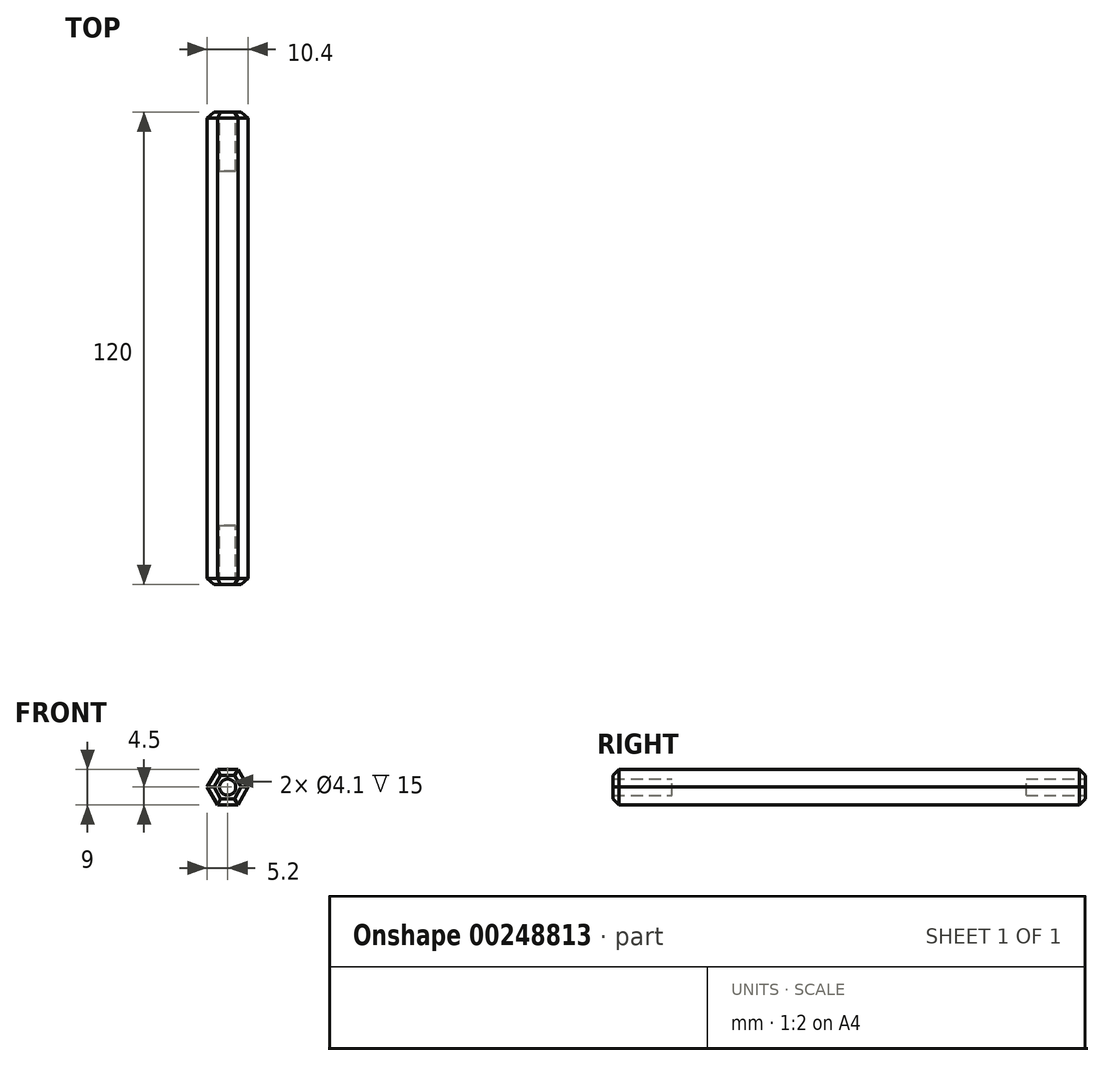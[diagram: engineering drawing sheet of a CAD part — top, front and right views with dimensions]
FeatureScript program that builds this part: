
annotation { "Feature Type Name" : "Feature", "Feature Type Description" : "" }
export const myFeature = defineFeature(function(context is Context, id is Id, definition is map)
    precondition{}
    {
        {
            assignVariable(context, id + "F0", {"name" : "length", "anyValue" : 120});
        }
        {
            var Q0;
            Q0=qCreatedBy(makeId("Front.planeOp"),FACE);
            var sketch = newSketch(context, id + "F1", { "sketchPlane" : qUnion([Q0])});
            skCircle(sketch, "E0.cCircle", {"center": v(0, 0) * mm, "radius": 4.5 * mm, "construction": true});
            skLineSegment(sketch, "E0.0", {"start": v(2.6, -4.5) * mm, "end": v(-2.6, -4.5) * mm});
            skLineSegment(sketch, "E0.1", {"start": v(-2.6, -4.5) * mm, "end": v(-5.2, 0) * mm});
            skLineSegment(sketch, "E0.2", {"start": v(-5.2, 0) * mm, "end": v(-2.6, 4.5) * mm});
            skLineSegment(sketch, "E0.3", {"start": v(-2.6, 4.5) * mm, "end": v(2.6, 4.5) * mm});
            skLineSegment(sketch, "E0.4", {"start": v(2.6, 4.5) * mm, "end": v(5.2, 0) * mm});
            skLineSegment(sketch, "E0.5", {"start": v(5.2, 0) * mm, "end": v(2.6, -4.5) * mm});
            skPoint(sketch, "E0.0.midPoint", {"position": v(0, -4.5) * mm});
            skCircle(sketch, "E1", {"center": v(0, 0) * mm, "radius": 2.05 * mm});
            skSolve(sketch);
        }
        {
            var Q0;
            Q0=makeQuery(id+"F1.imprint","IMPRINT",FACE,{"disambiguationData":[TD([[makeQuery(id+"F1.imprint","IMPRINT",EDGE,{"derivedFrom":sQuery(id+"F1.wireOp",EDGE,"E0.0")}),-1.0]])]});
            extrude(context, id + "F2", {"entities" : qUnion([Q0]), "depth" : (getVariable(context, 'length')) * mm, "symmetric" : true});
        }
        {
            var Q0;
            Q0=makeQuery(id+"F1.imprint","IMPRINT",FACE,{"disambiguationData":[TD([[makeQuery(id+"F1.imprint","IMPRINT",EDGE,{"derivedFrom":sQuery(id+"F1.wireOp",EDGE,"E1")}),1.0]])]});
            extrude(context, id + "F3", {"entities" : qUnion([Q0]), "operationType" : NewBodyOperationType.ADD, "depth" : (getVariable(context, 'length') - 30) * mm, "symmetric" : true});
        }
        {
            var Q0;
            Q0=makeQuery(id+"F2.opExtrude","CAP_EDGE",EDGE,{"disambiguationData":[OSD([sQuery(id+"F1.wireOp",EDGE,"E0.4")])],"isStart":false});
            var Q1;
            Q1=makeQuery(id+"F2.opExtrude","CAP_EDGE",EDGE,{"disambiguationData":[OSD([sQuery(id+"F1.wireOp",EDGE,"E0.3")])],"isStart":false});
            var Q2;
            Q2=makeQuery(id+"F2.opExtrude","CAP_EDGE",EDGE,{"disambiguationData":[OSD([sQuery(id+"F1.wireOp",EDGE,"E0.2")])],"isStart":false});
            var Q3;
            Q3=makeQuery(id+"F2.opExtrude","CAP_EDGE",EDGE,{"disambiguationData":[OSD([sQuery(id+"F1.wireOp",EDGE,"E0.1")])],"isStart":false});
            var Q4;
            Q4=makeQuery(id+"F2.opExtrude","CAP_EDGE",EDGE,{"disambiguationData":[OSD([sQuery(id+"F1.wireOp",EDGE,"E0.0")])],"isStart":false});
            var Q5;
            Q5=makeQuery(id+"F2.opExtrude","CAP_EDGE",EDGE,{"disambiguationData":[OSD([sQuery(id+"F1.wireOp",EDGE,"E0.5")])],"isStart":false});
            var Q6;
            Q6=makeQuery(id+"F2.opExtrude","CAP_EDGE",EDGE,{"disambiguationData":[OSD([sQuery(id+"F1.wireOp",EDGE,"E0.4")])],"isStart":true});
            var Q7;
            Q7=makeQuery(id+"F2.opExtrude","CAP_EDGE",EDGE,{"disambiguationData":[OSD([sQuery(id+"F1.wireOp",EDGE,"E0.3")])],"isStart":true});
            var Q8;
            Q8=makeQuery(id+"F2.opExtrude","CAP_EDGE",EDGE,{"disambiguationData":[OSD([sQuery(id+"F1.wireOp",EDGE,"E0.2")])],"isStart":true});
            var Q9;
            Q9=makeQuery(id+"F2.opExtrude","CAP_EDGE",EDGE,{"disambiguationData":[OSD([sQuery(id+"F1.wireOp",EDGE,"E0.1")])],"isStart":true});
            var Q10;
            Q10=makeQuery(id+"F2.opExtrude","CAP_EDGE",EDGE,{"disambiguationData":[OSD([sQuery(id+"F1.wireOp",EDGE,"E0.0")])],"isStart":true});
            var Q11;
            Q11=makeQuery(id+"F2.opExtrude","CAP_EDGE",EDGE,{"disambiguationData":[OSD([sQuery(id+"F1.wireOp",EDGE,"E0.5")])],"isStart":true});
            chamfer(context, id + "F4", {"entities" : qUnion([Q0, Q1, Q2, Q3, Q4, Q5, Q6, Q7, Q8, Q9, Q10, Q11]), "width" : 1.5 * mm, "tangentPropagation" : true});
        }
    });
